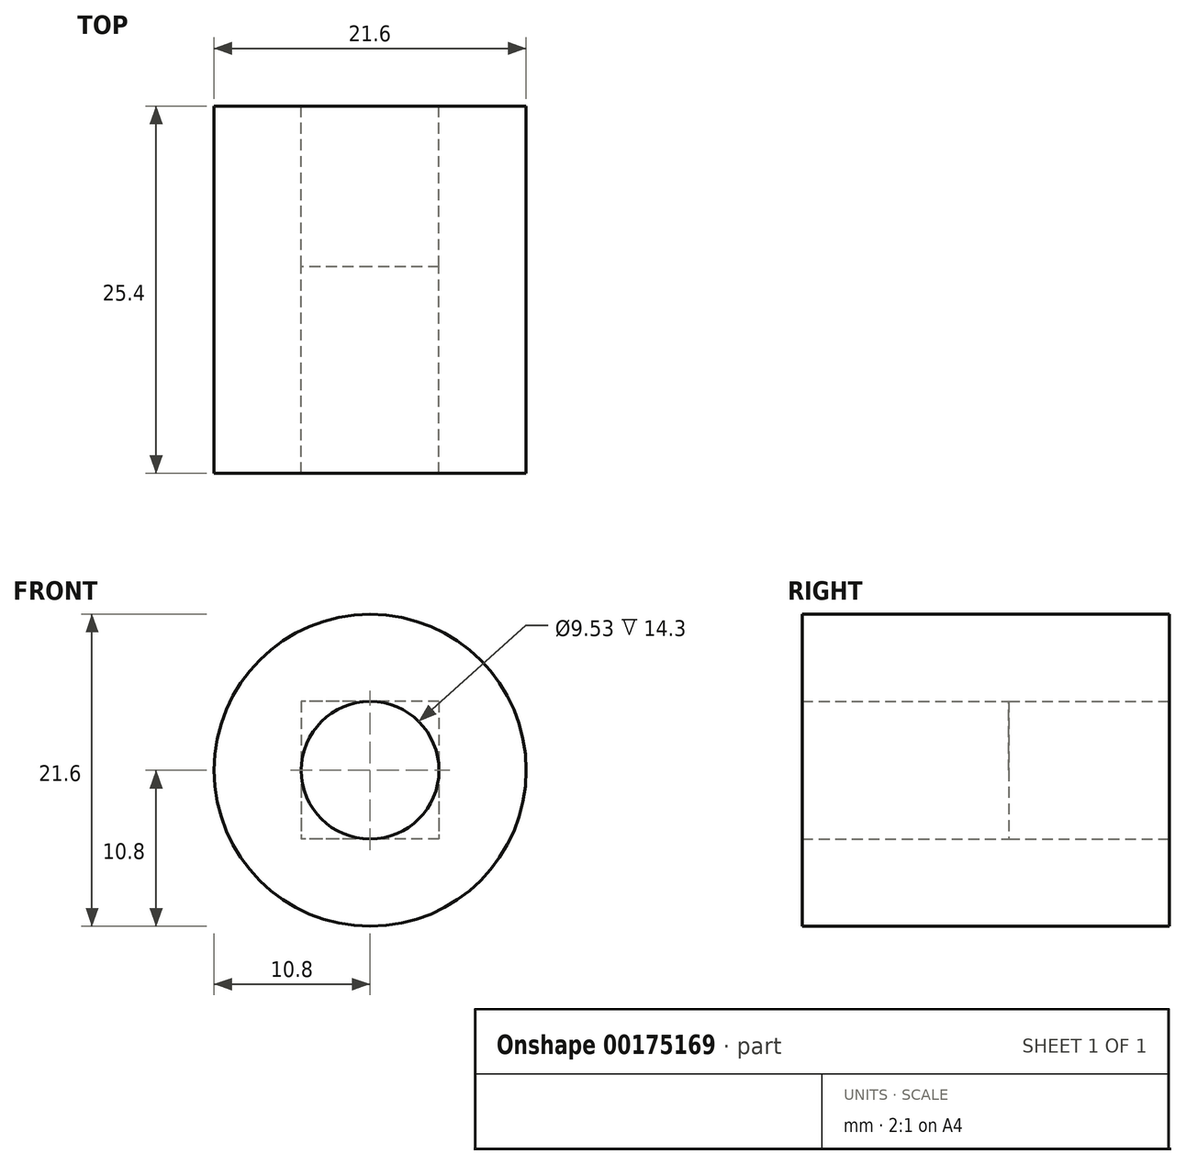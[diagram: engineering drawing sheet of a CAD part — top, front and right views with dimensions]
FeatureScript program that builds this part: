
annotation { "Feature Type Name" : "Feature", "Feature Type Description" : "" }
export const myFeature = defineFeature(function(context is Context, id is Id, definition is map)
    precondition{}
    {
        {
            var Q0;
            Q0=qCreatedBy(makeId("Front.planeOp"),FACE);
            var sketch = newSketch(context, id + "F0", { "sketchPlane" : qUnion([Q0])});
            skCircle(sketch, "E0", {"center": v(0, 0) * mm, "radius": 10.8 * mm});
            skSolve(sketch);
        }
        {
            var Q0;
            Q0 = qSketchRegion(id + "F0", true);
            extrude(context, id + "F1", {"entities" : qUnion([Q0]), "depth" : 25.4 * mm});
        }
        {
            var Q0;
            Q0=qCreatedBy(makeId("Front.planeOp"),FACE);
            var sketch = newSketch(context, id + "F2", { "sketchPlane" : qUnion([Q0])});
            skLineSegment(sketch, "E1.bottom", {"start": v(4.76, 4.76) * mm, "end": v(-4.76, 4.76) * mm});
            skLineSegment(sketch, "E1.top", {"start": v(4.76, -4.76) * mm, "end": v(-4.76, -4.76) * mm});
            skLineSegment(sketch, "E1.left", {"start": v(4.76, 4.76) * mm, "end": v(4.76, -4.76) * mm});
            skLineSegment(sketch, "E1.right", {"start": v(-4.76, 4.76) * mm, "end": v(-4.76, -4.76) * mm});
            skPoint(sketch, "E1.middle", {"position": v(0, 0) * mm});
            skCircle(sketch, "E2", {"center": v(0, 0) * mm, "radius": 4.76 * mm});
            skSolve(sketch);
        }
        {
            var Q0;
            {var subQ0=sQuery(id+"F2.wireOp",EDGE,"E2");var subQ1=makeQuery(id+"F2.imprint","INTERSECT",VERTEX,{"derivedFrom":[sQuery(id+"F2.wireOp",EDGE,"E1.bottom"),subQ0]});Q0=makeQuery(id+"F2.imprint","IMPRINT",FACE,{"disambiguationData":[TD([[makeQuery(id+"F2.imprint","IMPRINT",EDGE,{"disambiguationData":[TD([[subQ1,1.0]])],"derivedFrom":subQ0}),1.0]])]});}
            extrude(context, id + "F3", {"entities" : qUnion([Q0]), "operationType" : NewBodyOperationType.REMOVE, "endBound" : BoundingType.THROUGH_ALL, "depth" : 25.4 * mm});
        }
        {
            var Q0;
            Q0 = qSketchRegion(id + "F2", true);
            extrude(context, id + "F4", {"entities" : qUnion([Q0]), "operationType" : NewBodyOperationType.REMOVE, "depth" : 11.1 * mm});
        }
    });
